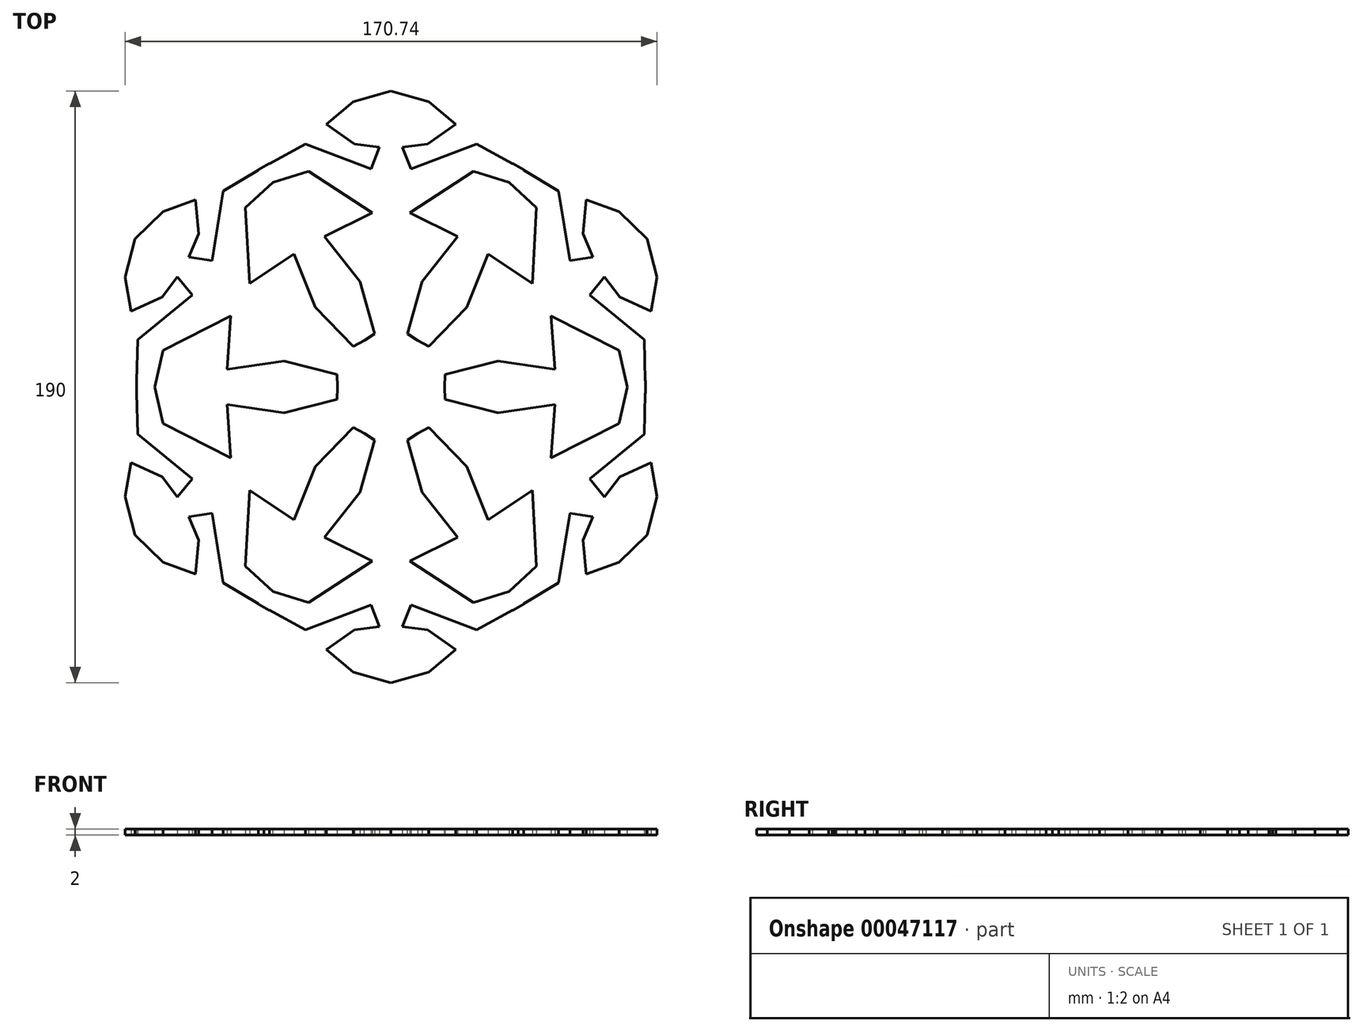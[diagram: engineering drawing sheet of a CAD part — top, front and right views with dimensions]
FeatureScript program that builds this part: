
annotation { "Feature Type Name" : "Feature", "Feature Type Description" : "" }
export const myFeature = defineFeature(function(context is Context, id is Id, definition is map)
    precondition{}
    {
        {
            var Q0;
            Q0=qCreatedBy(makeId("Top.planeOp"),FACE);
            var sketch = newSketch(context, id + "F0", { "sketchPlane" : qUnion([Q0])});
            skLineSegment(sketch, "E0", {"start": v(0, 0) * mm, "end": v(0, 95) * mm, "construction": true});
            skLineSegment(sketch, "E1", {"start": v(0, 0) * mm, "end": v(9.1, 0) * mm});
            skLineSegment(sketch, "E2", {"start": v(9.1, 0) * mm, "end": v(15, 11.6) * mm});
            skLineSegment(sketch, "E3", {"start": v(15, 11.6) * mm, "end": v(5.12, 16.64) * mm});
            skLineSegment(sketch, "E4", {"start": v(5.12, 16.64) * mm, "end": v(9.97, 33.87) * mm});
            skLineSegment(sketch, "E5", {"start": v(9.97, 33.87) * mm, "end": v(21.44, 48.38) * mm});
            skLineSegment(sketch, "E6", {"start": v(21.44, 48.38) * mm, "end": v(6.03, 55.91) * mm});
            skLineSegment(sketch, "E7", {"start": v(6.03, 55.91) * mm, "end": v(26.47, 69.23) * mm});
            skLineSegment(sketch, "E8", {"start": v(26.47, 69.23) * mm, "end": v(38.86, 65.46) * mm});
            skLineSegment(sketch, "E9", {"start": v(38.86, 65.46) * mm, "end": v(42.63, 69.76) * mm});
            skLineSegment(sketch, "E10", {"start": v(42.63, 69.76) * mm, "end": v(27.54, 78.07) * mm});
            skLineSegment(sketch, "E11", {"start": v(27.54, 78.07) * mm, "end": v(6.37, 70.02) * mm});
            skLineSegment(sketch, "E12", {"start": v(6.37, 70.02) * mm, "end": v(3.7, 77.06) * mm});
            skLineSegment(sketch, "E13", {"start": v(3.7, 77.06) * mm, "end": v(11.76, 78.07) * mm});
            skLineSegment(sketch, "E14", {"start": v(11.76, 78.07) * mm, "end": v(20.72, 84.4) * mm});
            skLineSegment(sketch, "E15", {"start": v(20.72, 84.4) * mm, "end": v(12.12, 91.58) * mm});
            skLineSegment(sketch, "E16", {"start": v(12.12, 91.58) * mm, "end": v(0, 95) * mm});
            skLineSegment(sketch, "E17", {"start": v(0, 0) * mm, "end": v(0, 95) * mm});
            skSolve(sketch);
        }
        {
            var Q0;
            Q0=qSketchRegion(id+"F0",true);
            extrude(context, id + "F1", {"entities" : qUnion([Q0]), "depth" : 2 * mm});
        }
        {
            var Q0;
            Q0=makeQuery(id+"F1.opExtrude","SWEPT_BODY",BODY,{"disambiguationData":[OSD([sQuery(id+"F0.wireOp",EDGE,"E1"),sQuery(id+"F0.wireOp",EDGE,"E2"),sQuery(id+"F0.wireOp",EDGE,"E3"),sQuery(id+"F0.wireOp",EDGE,"E4"),sQuery(id+"F0.wireOp",EDGE,"E5"),sQuery(id+"F0.wireOp",EDGE,"E6"),sQuery(id+"F0.wireOp",EDGE,"E7"),sQuery(id+"F0.wireOp",EDGE,"E8"),sQuery(id+"F0.wireOp",EDGE,"E9"),sQuery(id+"F0.wireOp",EDGE,"E10"),sQuery(id+"F0.wireOp",EDGE,"E11"),sQuery(id+"F0.wireOp",EDGE,"E12"),sQuery(id+"F0.wireOp",EDGE,"E13"),sQuery(id+"F0.wireOp",EDGE,"E14"),sQuery(id+"F0.wireOp",EDGE,"E15"),sQuery(id+"F0.wireOp",EDGE,"E16"),sQuery(id+"F0.wireOp",EDGE,"E17")])]});
            var Q1;
            Q1=qCreatedBy(makeId("Right.planeOp"),FACE);
            mirror(context, id + "F2", {"operationType" : NewBodyOperationType.ADD, "entities" : qUnion([Q0]), "mirrorPlane" : qUnion([Q1])});
        }
        {
            var Q0;
            Q0=qCreatedBy(makeId("Front.planeOp"),FACE);
            var sketch = newSketch(context, id + "F3", { "sketchPlane" : qUnion([Q0])});
            skLineSegment(sketch, "E18", {"start": v(0, 0) * mm, "end": v(0, 8.23) * mm});
            skSolve(sketch);
        }
        {
            var Q0;
            Q0=makeQuery(id+"F1.opExtrude","SWEPT_BODY",BODY,{"disambiguationData":[OSD([sQuery(id+"F0.wireOp",EDGE,"E1"),sQuery(id+"F0.wireOp",EDGE,"E2"),sQuery(id+"F0.wireOp",EDGE,"E3"),sQuery(id+"F0.wireOp",EDGE,"E4"),sQuery(id+"F0.wireOp",EDGE,"E5"),sQuery(id+"F0.wireOp",EDGE,"E6"),sQuery(id+"F0.wireOp",EDGE,"E7"),sQuery(id+"F0.wireOp",EDGE,"E8"),sQuery(id+"F0.wireOp",EDGE,"E9"),sQuery(id+"F0.wireOp",EDGE,"E10"),sQuery(id+"F0.wireOp",EDGE,"E11"),sQuery(id+"F0.wireOp",EDGE,"E12"),sQuery(id+"F0.wireOp",EDGE,"E13"),sQuery(id+"F0.wireOp",EDGE,"E14"),sQuery(id+"F0.wireOp",EDGE,"E15"),sQuery(id+"F0.wireOp",EDGE,"E16"),sQuery(id+"F0.wireOp",EDGE,"E17")])]});
            var Q1;
            Q1=sQuery(id+"F3.wireOp",EDGE,"E18");
            circularPattern(context, id + "F4", {"operationType" : NewBodyOperationType.ADD, "entities" : qUnion([Q0]), "axis" : qUnion([Q1]), "angle" : 60 * degree, "instanceCount" : round(6)});
        }
    });
